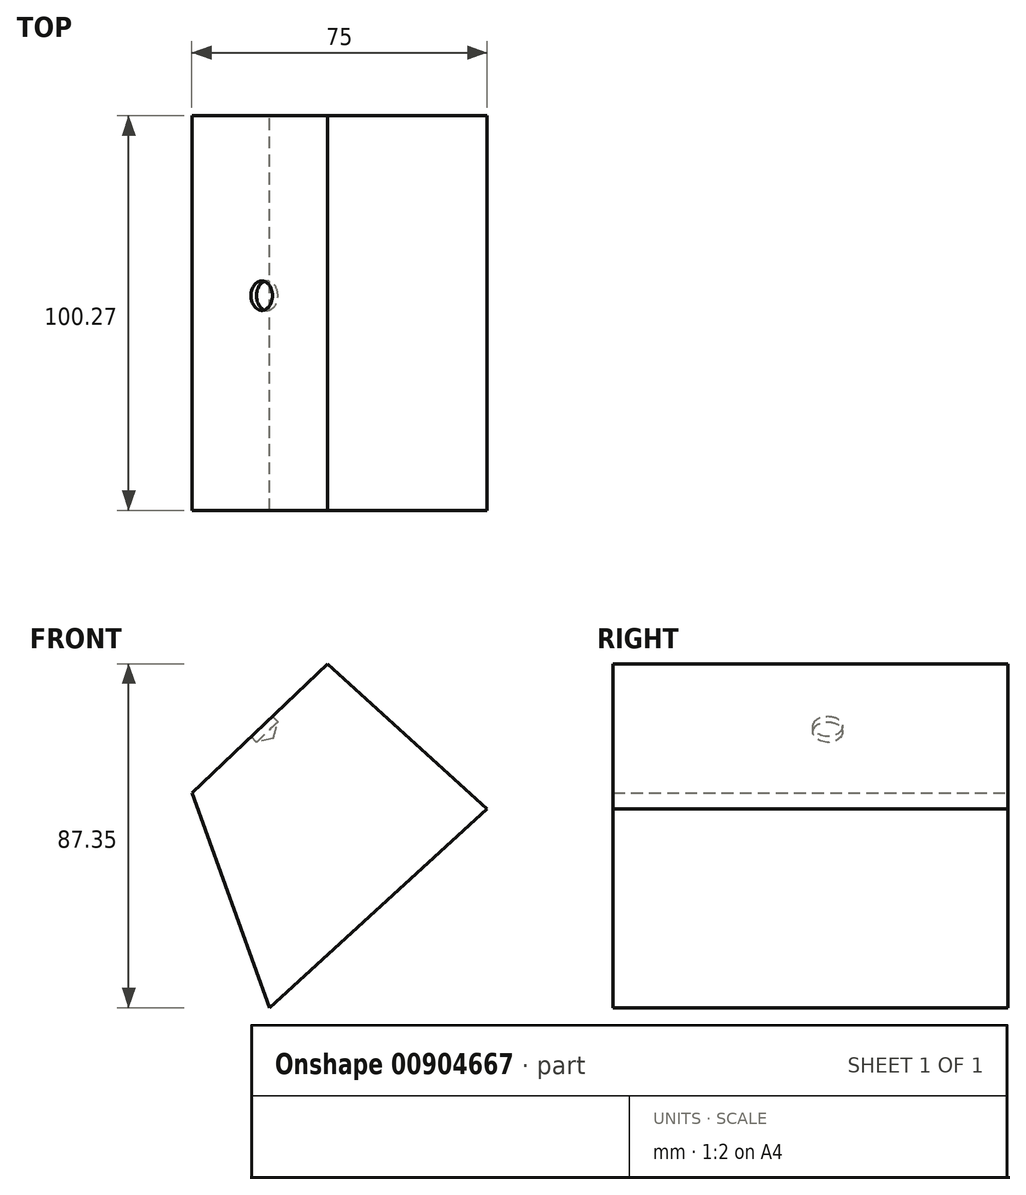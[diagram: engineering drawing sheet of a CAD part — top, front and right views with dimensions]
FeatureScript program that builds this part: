
annotation { "Feature Type Name" : "Feature", "Feature Type Description" : "" }
export const myFeature = defineFeature(function(context is Context, id is Id, definition is map)
    precondition{}
    {
        {
            var Q0;
            Q0=qCreatedBy(makeId("Front.planeOp"),FACE);
            var sketch = newSketch(context, id + "F0", { "sketchPlane" : qUnion([Q0])});
            skLineSegment(sketch, "E0", {"start": v(-47.56, 45.08) * mm, "end": v(0, 0) * mm});
            skLineSegment(sketch, "E1", {"start": v(0, 0) * mm, "end": v(27.95, 41.48) * mm});
            skLineSegment(sketch, "E2", {"start": v(27.95, 41.48) * mm, "end": v(-12.61, 78.35) * mm});
            skLineSegment(sketch, "E3", {"start": v(-12.61, 78.35) * mm, "end": v(-47.56, 45.08) * mm});
            skLineSegment(sketch, "E4", {"start": v(-27.27, -9.07) * mm, "end": v(0, 0) * mm});
            skLineSegment(sketch, "E5", {"start": v(-47.05, 45.57) * mm, "end": v(-27.27, -9.07) * mm});
            skLineSegment(sketch, "E6", {"start": v(-27.95, -9.6) * mm, "end": v(27.95, 41.48) * mm});
            skSolve(sketch);
        }
        {
            var Q0;
            {var subQ0=sQuery(id+"F0.wireOp",EDGE,"E5");var subQ1=sQuery(id+"F0.wireOp",EDGE,"E0");var subQ2=makeQuery(id+"F0.imprint","INTERSECT",VERTEX,{"derivedFrom":[subQ1,subQ0]});Q0=makeQuery(id+"F0.imprint","IMPRINT",FACE,{"disambiguationData":[TD([[makeQuery(id+"F0.imprint","IMPRINT",EDGE,{"disambiguationData":[TD([[subQ2,-1.0]])],"derivedFrom":subQ1}),-1.0]])]});}
            var Q1;
            {var subQ5=sQuery(id+"F0.wireOp",EDGE,"E2");Q1=makeQuery(id+"F0.imprint","IMPRINT",FACE,{"disambiguationData":[TD([[makeQuery(id+"F0.imprint","IMPRINT",EDGE,{"derivedFrom":subQ5}),1.0]])]});}
            extrude(context, id + "F1", {"entities" : qUnion([Q0, Q1]), "depth" : 100.27 * mm, "offsetDistance" : 25 * mm});
        }
        {
            var Q0;
            Q0=makeQuery(id+"F1.opExtrude","SWEPT_FACE",FACE,{"disambiguationData":[OSD([sQuery(id+"F0.wireOp",EDGE,"E3")])]});
            var sketch = newSketch(context, id + "F2", { "sketchPlane" : qUnion([Q0])});
            skPoint(sketch, "E7", {"position": v(21.87, -45.71) * mm});
            skSolve(sketch);
        }
        {
            var Q0;
            Q0=sQuery(id+"F2.wireOp",VERTEX,"E7");
            var Q1;
            Q1=makeQuery(id+"F1.opExtrude","SWEPT_BODY",BODY,{"disambiguationData":[OSD([sQuery(id+"F0.wireOp",EDGE,"E2"),sQuery(id+"F0.wireOp",EDGE,"E3"),sQuery(id+"F0.wireOp",EDGE,"E5"),sQuery(id+"F0.wireOp",EDGE,"E6")])]});
            hole(context, id + "F3", {"style" : HoleStyle.SIMPLE, "endStyle" : HoleEndStyle.BLIND, "holeDiameter" : 7.5 * mm, "majorDiameter" : 5 * mm, "holeDepth" : 2 * mm, "isTappedThrough" : true, "tappedDepth" : 12 * mm, "tapClearance" : 3, "locations" : qUnion([Q0]), "scope" : qUnion([Q1])});
        }
    });
